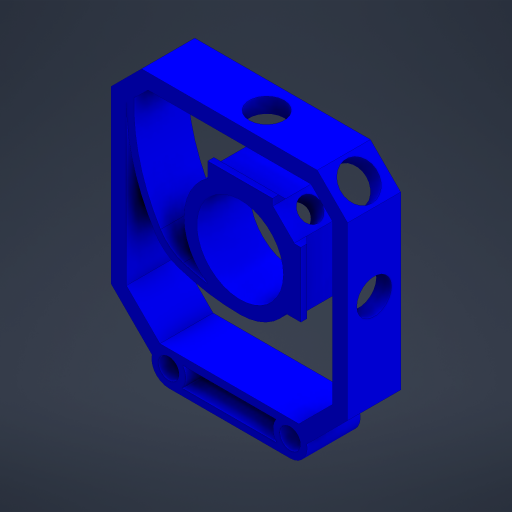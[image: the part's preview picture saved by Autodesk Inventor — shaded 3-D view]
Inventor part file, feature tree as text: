
AUTODESK INVENTOR PART (.ipt)
format: ipt  version: 2023.4 (Build 274418000, 418)  size: 509,952 bytes
history: native  units: mm
features: extrude x6, projected_geometry x4, reference x4, other x3, plane x1, mirror x1, sketch x1
ambient origin geometry x8: Origin, YZ Plane, XZ Plane, XY Plane, X Axis, Y Axis, Z Axis, Center Point
bodies: Solid1 (feature_tree)
feature tree (20):
  extrude  "Extrusion1"  TaperAngle=45.0deg  [1 undecoded]
  extrude  "Extrusion2"  Depth=10.0mm
  extrude  "Extrusion3"  Depth=10.0mm
  extrude  "Extrusion4"  Depth=10.0mm
  plane  "Work Plane1"
  mirror  "Mirror1"
  extrude  "Extrusion5"  Depth=10.0mm
  extrude  "Extrusion6"  Depth=10.0mm
  sketch  "Sketch1"  dims[d2=2.5mm d3=45.0deg d4=14.25mm d5=0.675mm d6=2.125mm d7=0.5mm d8=10.675mm d9=2.5mm d10=0.625mm d11=5.0mm d12=135.0deg d13=3.0mm d14=2.0mm d15=2.0mm d16=38.935534mm d17=38.935534mm d18=9.25mm d19=9.25mm d20=9.25mm d21=9.25mm d22=5.0mm d23=5.0mm d24=5.0mm d25=5.0mm d26=2.5mm d28=8.75mm d29=0.0mm d30=0.875mm d31=0.875mm d32=0.0mm d33=5.75mm d34=10.0mm d35=0.0mm d36=1.0mm d37=135.0deg d38=10.0mm d39=0.0mm d40=3.75mm d41=6.0mm d42=5.0mm d43=0.0mm d44=10.0mm d45=0.0mm d46=2.5mm d50=12.5mm d51=2.5mm d52=1.25mm d53=2.5mm d54=2.5mm d61=1.25mm d62=1.25mm d63=0.1425mm d64=0.1425mm]
  projected_geometry  "Projected Loop1"
  projected_geometry  "Projected Loop2"
  projected_geometry  "Projected Loop4"
  projected_geometry  "Projected Loop5"
  reference  "Reference4"
  reference  "Reference5"
  reference  "Reference6"
  reference  "Reference7"
  other  "<path>\Projects\Project Protocube\Protocube\CAD, STL, OBJ Files\1 CAD\Cube 1x1 V5.iam"
  other  "Cube 1x1 V5.iam"
  other  "Cube 1x1 Bottom V5 Closed Slotted:1"
note: 1 required parameter value undecoded (feature->parameter linkage not recoverable at this tier; creation-order binding heuristic only, values carry confidence <= 0.55)
note: 1 file-system path scrubbed to <path> (originals preserved in map.json)
